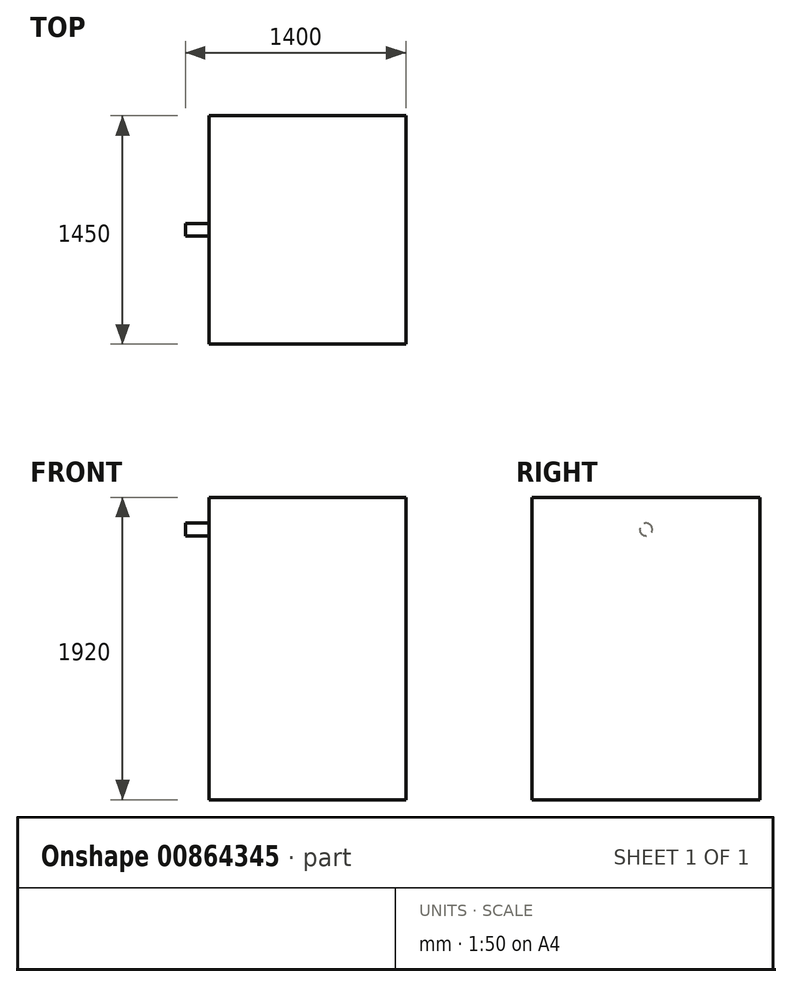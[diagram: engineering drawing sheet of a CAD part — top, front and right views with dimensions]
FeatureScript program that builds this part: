
annotation { "Feature Type Name" : "Feature", "Feature Type Description" : "" }
export const myFeature = defineFeature(function(context is Context, id is Id, definition is map)
    precondition{}
    {
        {
            var Q0;
            Q0=qCreatedBy(makeId("Top.planeOp"),FACE);
            var sketch = newSketch(context, id + "F0", { "sketchPlane" : qUnion([Q0])});
            skLineSegment(sketch, "E0.bottom", {"start": v(-1250, -1450) * mm, "end": v(0, -1450) * mm});
            skLineSegment(sketch, "E0.top", {"start": v(-1250, 0) * mm, "end": v(0, 0) * mm});
            skLineSegment(sketch, "E0.left", {"start": v(-1250, -1450) * mm, "end": v(-1250, 0) * mm});
            skLineSegment(sketch, "E0.right", {"start": v(0, -1450) * mm, "end": v(0, 0) * mm});
            skSolve(sketch);
        }
        {
            var Q0;
            Q0 = qSketchRegion(id + "F0", true);
            extrude(context, id + "F1", {"entities" : qUnion([Q0]), "depth" : 1920 * mm, "offsetDistance" : 25 * mm});
        }
        {
            var Q0;
            Q0=makeQuery(id+"F1.opExtrude","SWEPT_FACE",FACE,{"disambiguationData":[OSD([sQuery(id+"F0.wireOp",EDGE,"E0.left")])]});
            var sketch = newSketch(context, id + "F2", { "sketchPlane" : qUnion([Q0])});
            skCircle(sketch, "E1", {"center": v(725, 1717) * mm, "radius": 40 * mm});
            skPoint(sketch, "E1.centerSnap0", {"position": v(725, 1920) * mm});
            skSolve(sketch);
        }
        {
            var Q0;
            Q0=makeQuery(id+"F2.imprint","IMPRINT",FACE,{"disambiguationData":[TD([[makeQuery(id+"F2.imprint","IMPRINT",EDGE,{"derivedFrom":sQuery(id+"F2.wireOp",EDGE,"E1")}),1.0]])]});
            extrude(context, id + "F3", {"entities" : qUnion([Q0]), "operationType" : NewBodyOperationType.ADD, "depth" : 150 * mm, "offsetDistance" : 25 * mm});
        }
    });
